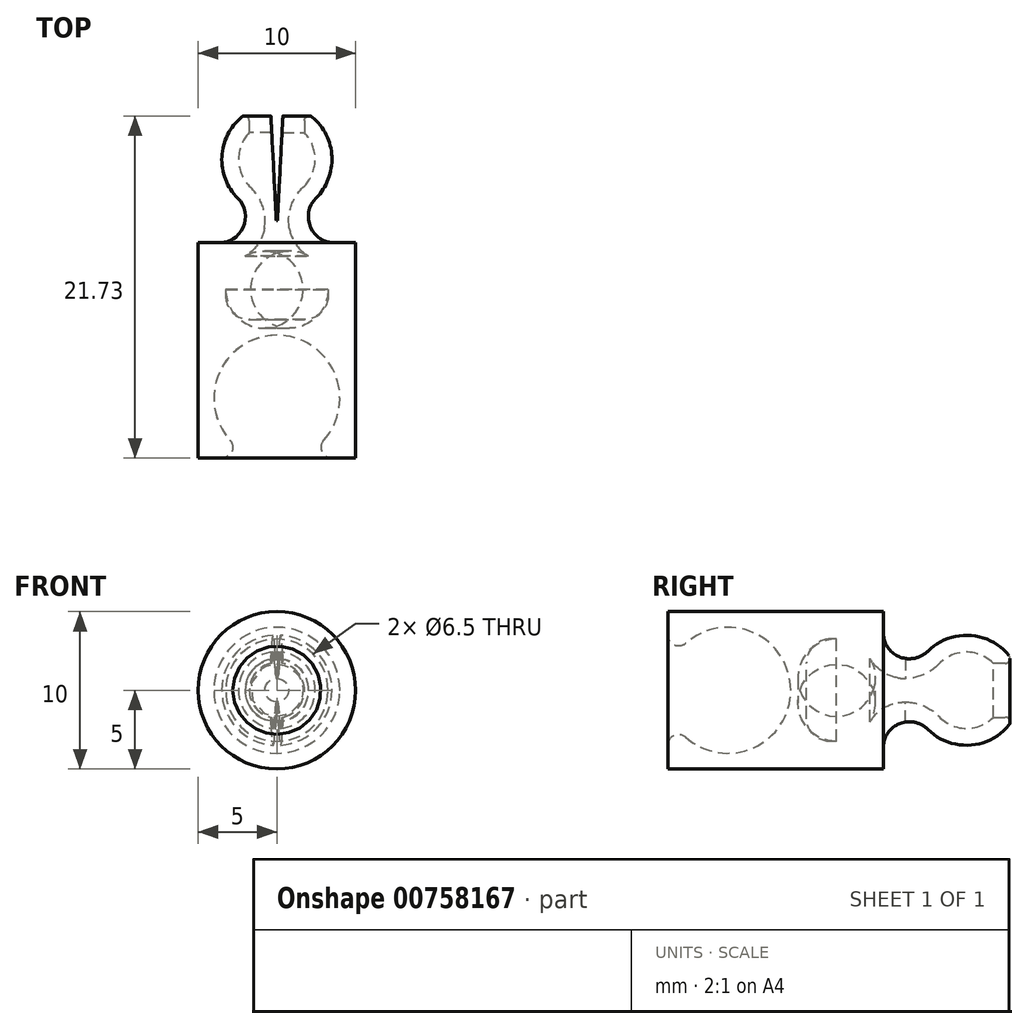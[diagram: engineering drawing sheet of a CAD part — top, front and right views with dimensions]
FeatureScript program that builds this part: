
annotation { "Feature Type Name" : "Feature", "Feature Type Description" : "" }
export const myFeature = defineFeature(function(context is Context, id is Id, definition is map)
    precondition{}
    {
        {
            var Q0;
            Q0=qCreatedBy(makeId("Top.planeOp"),FACE);
            var sketch = newSketch(context, id + "F0", { "sketchPlane" : qUnion([Q0])});
            skLineSegment(sketch, "E0", {"start": v(0, 0) * mm, "end": v(0, 38.07) * mm, "construction": true});
            skLineSegment(sketch, "E1", {"start": v(-33.52, 0) * mm, "end": v(40.8, 0) * mm, "construction": true});
            skLineSegment(sketch, "E2", {"start": v(-5, 18.1) * mm, "end": v(-5, 4.43) * mm});
            skArc(sketch, "E3", {"start": v(-1.75, 26.43) * mm, "mid": v(-3.47, 23.86) * mm, "end": v(-2.48, 20.93) * mm});
            skLineSegment(sketch, "E4", {"start": v(-5, 18.1) * mm, "end": v(-3.66, 18.1) * mm});
            skArc(sketch, "E5", {"start": v(-3.66, 18.1) * mm, "mid": v(-2.13, 19.13) * mm, "end": v(-2.48, 20.93) * mm});
            skLineSegment(sketch, "E6", {"start": v(-3.47, 19.6) * mm, "end": v(-5, 19.6) * mm});
            skLineSegment(sketch, "E7", {"start": v(-5, 19.6) * mm, "end": v(-5, 34.8) * mm});
            skArc(sketch, "E8", {"start": v(-3.47, 19.6) * mm, "mid": v(-2.86, 20) * mm, "end": v(-2.97, 20.73) * mm});
            skArc(sketch, "E9", {"start": v(0, 27.4) * mm, "mid": v(-3.65, 25.03) * mm, "end": v(-2.97, 20.73) * mm});
            skArc(sketch, "E10", {"start": v(-1.75, 25.1) * mm, "mid": v(-2.43, 23.35) * mm, "end": v(-1.67, 21.63) * mm});
            skLineSegment(sketch, "E11", {"start": v(0, 20.8) * mm, "end": v(0, 12.23) * mm});
            skLineSegment(sketch, "E12", {"start": v(-2, 20.44) * mm, "end": v(-2, 17.88) * mm, "construction": true});
            skArc(sketch, "E13", {"start": v(-1.67, 21.63) * mm, "mid": v(-0.9, 20.45) * mm, "end": v(-0.78, 19.05) * mm});
            skArc(sketch, "E14", {"start": v(-0.78, 19.05) * mm, "mid": v(-1.2, 18.02) * mm, "end": v(-2.01, 17.27) * mm});
            skArc(sketch, "E15", {"start": v(-2.01, 17.27) * mm, "mid": v(-2.92, 16.37) * mm, "end": v(-3.25, 15.13) * mm});
            skLineSegment(sketch, "E16", {"start": v(-3.25, 15.13) * mm, "end": v(-3.25, 14.73) * mm});
            skLineSegment(sketch, "E17", {"start": v(-0.75, 20.05) * mm, "end": v(-0.75, 17.72) * mm, "construction": true});
            skLineSegment(sketch, "E18", {"start": v(-5, 4.43) * mm, "end": v(-3.47, 4.43) * mm});
            skArc(sketch, "E19", {"start": v(-3.47, 4.43) * mm, "mid": v(-2.86, 4.83) * mm, "end": v(-2.97, 5.55) * mm});
            skArc(sketch, "E20", {"start": v(-2.97, 5.55) * mm, "mid": v(-3.65, 9.86) * mm, "end": v(0, 12.23) * mm});
            skArc(sketch, "E21", {"start": v(-3.25, 14.73) * mm, "mid": v(-2.81, 13.67) * mm, "end": v(-1.75, 13.23) * mm});
            skLineSegment(sketch, "E22", {"start": v(-1.75, 13.23) * mm, "end": v(0, 13.23) * mm});
            skLineSegment(sketch, "E23", {"start": v(-2.84, 12.23) * mm, "end": v(3.02, 12.23) * mm, "construction": true});
            skLineSegment(sketch, "E24", {"start": v(-1.75, 25.1) * mm, "end": v(-1.75, 26.43) * mm});
            skLineSegment(sketch, "E25", {"start": v(-2.8, 2.77) * mm, "end": v(-2.8, 28.85) * mm, "construction": true});
            skLineSegment(sketch, "E26", {"start": v(-3.76, 27.4) * mm, "end": v(4.3, 27.4) * mm, "construction": true});
            skLineSegment(sketch, "E27", {"start": v(-4, 2.8) * mm, "end": v(-4, 30.04) * mm, "construction": true});
            skSolve(sketch);
        }
        {
            var Q0;
            Q0=makeQuery(id+"F0.imprint","IMPRINT",FACE,{"disambiguationData":[TD([[makeQuery(id+"F0.imprint","IMPRINT",EDGE,{"derivedFrom":sQuery(id+"F0.wireOp",EDGE,"E2")}),1.0]])]});
            var Q1;
            Q1=sQuery(id+"F0.wireOp",EDGE,"E0");
            revolve(context, id + "F1", {"surfaceOperationType" : NewSurfaceOperationType.NEW, "entities" : qUnion([Q0]), "axis" : qUnion([Q1]), "revolveType" : RevolveType.FULL});
        }
        {
            var Q0;
            Q0=makeQuery(id+"F1.opRevolve","SWEPT_EDGE",EDGE,{"disambiguationData":[OSD([sQuery(id+"F0.wireOp",EDGE,"E3"),sQuery(id+"F0.wireOp",EDGE,"E24")])]});
            fillet(context, id + "F2", {"entities" : qUnion([Q0]), "radius" : 0.3 * mm, "tangentPropagation" : true, "allowEdgeOverflow" : false});
        }
        {
            var Q0;
            Q0=qCreatedBy(makeId("Front.planeOp"),FACE);
            cPlane(context, id + "F3", {"entities" : qUnion([Q0]), "cplaneType" : CPlaneType.OFFSET, "offset" : 26.5 * mm, "oppositeDirection" : true, "width" : 150 * mm, "height" : 150 * mm});
        }
        {
            var Q0;
            Q0=qCreatedBy(id+"F3.planeOp",FACE);
            var sketch = newSketch(context, id + "F4", { "sketchPlane" : qUnion([Q0])});
            skLineSegment(sketch, "E28.bottom", {"start": v(0.4, -5) * mm, "end": v(-0.4, -5) * mm});
            skLineSegment(sketch, "E28.top", {"start": v(0.4, 5) * mm, "end": v(-0.4, 5) * mm});
            skLineSegment(sketch, "E28.left", {"start": v(0.4, -5) * mm, "end": v(0.4, 5) * mm});
            skLineSegment(sketch, "E28.right", {"start": v(-0.4, -5) * mm, "end": v(-0.4, 5) * mm});
            skSolve(sketch);
        }
        {
            var Q0;
            Q0=makeQuery(id+"F4.imprint","IMPRINT",FACE,{"disambiguationData":[TD([[makeQuery(id+"F4.imprint","IMPRINT",EDGE,{"derivedFrom":sQuery(id+"F4.wireOp",EDGE,"E28.bottom")}),-1.0]])]});
            extrude(context, id + "F5", {"entities" : qUnion([Q0]), "operationType" : NewBodyOperationType.REMOVE, "depth" : 7 * mm, "offsetDistance" : 25 * mm, "hasDraft" : true, "draftAngle" : 3 * degree, "draftPullDirection" : true});
        }
    });
